# Revit family: tka-2400r2_60Hz
name_source: partatom
category: 機械設備
units: mm (PartAtom-declared; Revit-internal decimal feet)

## family parameters
OmniClass タイトル = Heat Exchangers for Ventilation Air
OmniClass 番号 = 23.75.10.34.21
パーツ タイプ = 標準
ロード時にボイドで切り取り = いいえ
丸型コネクタ寸法 = 直径を使用
作業面ベース = いいえ
共有 = いいえ
常に垂直 = はい
部屋計算ポイント = はい

## types (1)
- TKA-2400R2
    Box_D = 531  [stored 1.74213 ft]
    Box_Depth = 172  [stored 0.564304 ft]
    Box_H = 39  [stored 0.127953 ft]
    Box_Height = 262  [stored 0.85958 ft]
    Box_Width = 115  [stored 0.377297 ft]
    Clearance Left = 600
    Clearance Top = 340  [stored 1.11549 ft]
    Depth = 824  [stored 2.70341 ft]
    Duct_Depth = 84  [stored 0.275591 ft]
    Duct_Height = 134
    Duct_Width_RA = 130  [stored 0.426509 ft]
    Duct_Width_SA = 105  [stored 0.344488 ft]
    EAサイズ_D = 0  [stored 0 ft]
    EAサイズ_W = 0  [stored 0 ft]
    Height = 340  [stored 1.11549 ft]
    IfcExportAs = IfcAirToAirHeatRecoveryType
    IfcExportType = ROTARYWHEEL
    MAX静圧 = 95.0 Pa
    MAX風量 = 720.0 m³/h
    MID静圧 = 99.0 Pa
    MID風量 = 420.0 m³/h
    MIN静圧 = 24.0 Pa
    MIN風量 = 360.0 m³/h
    OAサイズ_D = 0  [stored 0 ft]
    OAサイズ_W = 0  [stored 0 ft]
    OmniClassCode = 23-27 23 19 11
    RAサイズ_D = 192  [stored 0.629921 ft]
    RAサイズ_W = 0  [stored 0 ft]
    SAサイズ_D = 192  [stored 0.629921 ft]
    SAサイズ_W = 0  [stored 0 ft]
    URL = https://www.mitsubishielectric.co.jp
    Uniclass2015Code = Pr_60_60_36_88
    Uniclass2015Title = Thermal wheels
    Uniclass2015Version = Systems v1.9
    Width = 692  [stored 2.27034 ft]
    エンタルピ交換効率_冷房 = 0.00%
    エンタルピ交換効率_暖房 = 0.00%
    ドレン管_D = 387  [stored 1.26969 ft]
    ドレン管_Depth = 20  [stored 0.0656168 ft]
    ドレン管_H = 20  [stored 0.0656168 ft]
    ドレン管径 = 32 mm
    メンテナンススペース = はい
    モデル = TKA-2400R2
    仕様書バージョン = Version1.0
    企業コード = 108420
    価格 = 244000 $
    冷媒ガス管径 = 13 mm
    冷媒液管径 = 6 mm
    分類コード = 50059009000999
    初期抵抗 = 0.0 Pa
    加湿給水管径 = 22 mm
    吊りボルト_高さ = 170  [stored 0.557743 ft]
    吊りボルトピッチ1 = 692  [stored 2.27034 ft]
    吊りボルトピッチ2 = 880  [stored 2.88714 ft]
    周波数 = 60 Hz
    呼称 = 加湿器
    外気量 = 0.0 m³/h
    天吊金具_幅 = 20  [stored 0.0656168 ft]
    天吊金具_径 = 7  [stored 0.0229659 ft]
    実風量 = 0.0 m³/h
    形式 = 滴下浸透気化式
    排気量 = 0.0 m³/h
    有効加湿量 = 2.4
    本体マテリアル = 溶融亜鉛めっき鋼板
    極数 = 2
    機外静圧 = 95.0 Pa
    機外静圧_排気 = 95.0 Pa
    法定耐用年数 = 15
    消費電力 = 201 W
    消費電力_加湿器 = 0 W
    温度交換効率 = 0.00%
    点検口 = はい
    点検口_Center = 412  [stored 1.35171 ft]
    点検口_Depth = 450  [stored 1.47638 ft]
    点検口_Width = 450  [stored 1.47638 ft]
    点検口離隔 = 150
    点検口高さ = -340  [stored -1.11549 ft]
    相 = 1
    積算_科目 = 1 空気調和設備
    符号 = HUM
    給水管_D = 395  [stored 1.29593 ft]
    給水管_Depth = 20  [stored 0.0656168 ft]
    給水管_H = 206  [stored 0.675853 ft]
    製品リリース年月 = 2016/2/1
    製品出荷対象 = 国内
    製品質量 = 33.00 kg
    製造元 = MITSUBISHI ELECTRIC
    設置方法 = 天井吊(隠ぺい)形
    設計風量 = 0.0 m³/h
    説明 = 業務用単独加湿ユニット
    負荷分類 = 3_ファン類
    質量 = 39.60 kg
    運転質量 = 0.00 kg
    電動機出力 = 0 W
    電圧 = 100 V
    面風速 = 6.4 m/s
    風量 = 720.0 m³/h
    騒音レベル(dB(A)) = 33.5

note: [stored X ft] marks values corroborated as IEEE doubles in the binary element streams (Revit-internal decimal feet)
